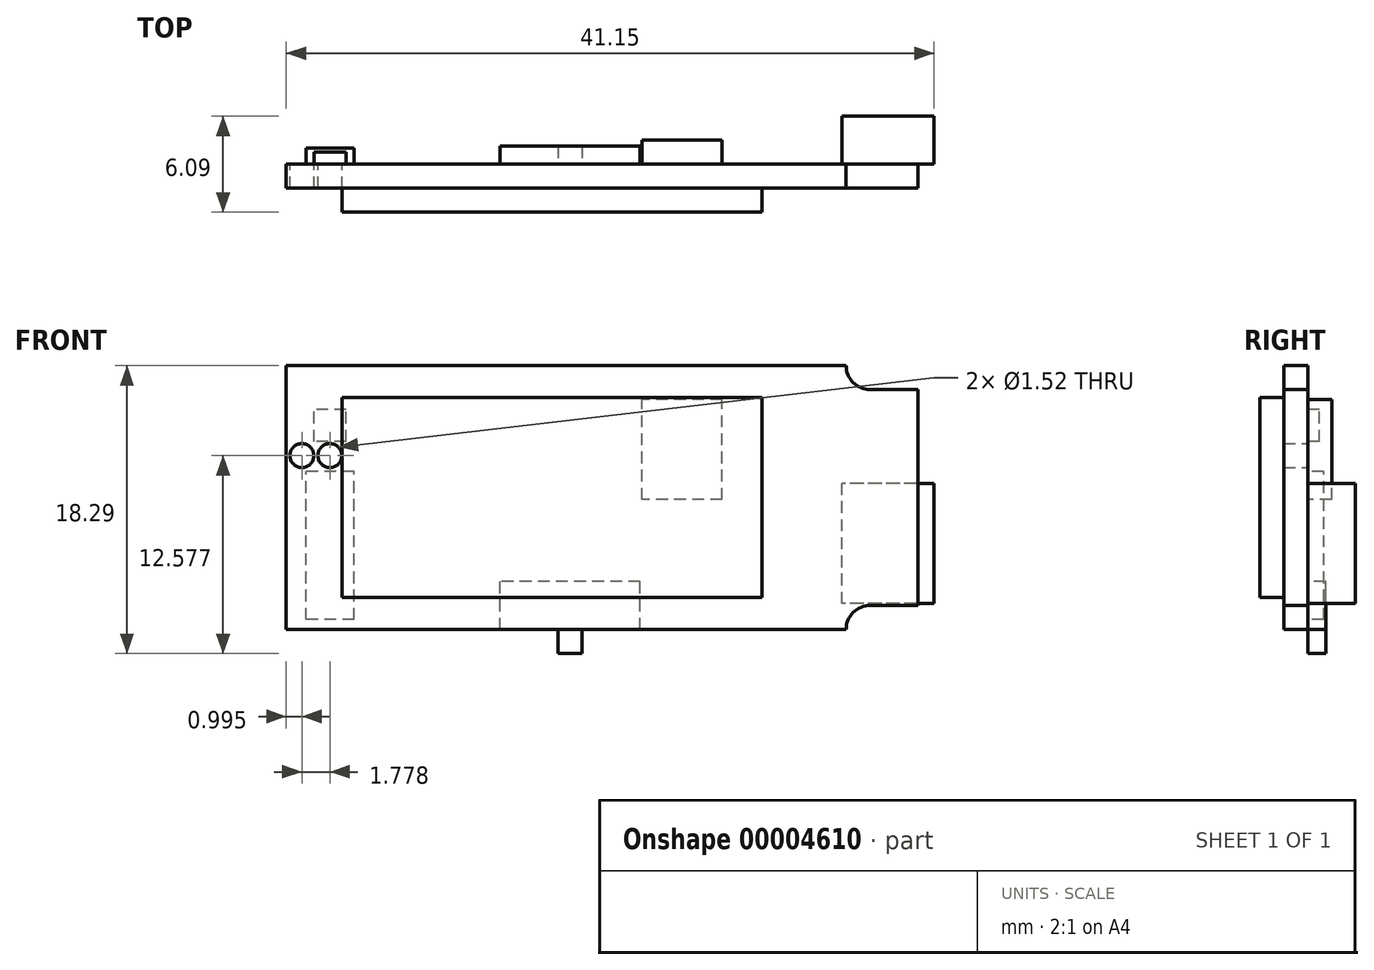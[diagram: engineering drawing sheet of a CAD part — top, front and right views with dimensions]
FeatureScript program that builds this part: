
annotation { "Feature Type Name" : "Feature", "Feature Type Description" : "" }
export const myFeature = defineFeature(function(context is Context, id is Id, definition is map)
    precondition{}
    {
        {
            var Q0;
            Q0=qCreatedBy(makeId("Front.planeOp"),FACE);
            var sketch = newSketch(context, id + "F0", { "sketchPlane" : qUnion([Q0])});
            skLineSegment(sketch, "E0.rect.bottom", {"start": v(20.07, -8.38) * mm, "end": v(-20.07, -8.38) * mm});
            skLineSegment(sketch, "E0.rect.top", {"start": v(20.07, 8.38) * mm, "end": v(-20.07, 8.38) * mm});
            skLineSegment(sketch, "E0.rect.left", {"start": v(20.07, -8.38) * mm, "end": v(20.07, 8.38) * mm});
            skLineSegment(sketch, "E0.rect.right", {"start": v(-20.07, -8.38) * mm, "end": v(-20.07, 8.38) * mm});
            skPoint(sketch, "E0.rect.middle", {"position": v(0, 0) * mm});
            skSolve(sketch);
        }
        {
            var Q0;
            Q0=makeQuery(id+"F0.imprint","IMPRINT",FACE,{"disambiguationData":[TD([[makeQuery(id+"F0.imprint","IMPRINT",EDGE,{"derivedFrom":sQuery(id+"F0.wireOp",EDGE,"E0.rect.bottom")}),-1.0]])]});
            extrude(context, id + "F1", {"entities" : qUnion([Q0]), "oppositeDirection" : true, "depth" : 1.52 * mm});
        }
        {
            var Q0;
            Q0=qCreatedBy(makeId("Front.planeOp"),FACE);
            var sketch = newSketch(context, id + "F2", { "sketchPlane" : qUnion([Q0])});
            skLineSegment(sketch, "E1.0", {"start": v(20.07, 6.86) * mm, "end": v(20.07, 8.38) * mm, "construction": true});
            skLineSegment(sketch, "E2.0", {"start": v(20.07, 8.38) * mm, "end": v(15.5, 8.38) * mm});
            skLineSegment(sketch, "E3", {"start": v(20.07, 6.86) * mm, "end": v(17.02, 6.86) * mm});
            skArc(sketch, "E4", {"start": v(15.5, 8.38) * mm, "mid": v(15.94, 7.3) * mm, "end": v(17.02, 6.86) * mm});
            skPoint(sketch, "E5.orphan", {"position": v(-20.07, 8.38) * mm});
            skPoint(sketch, "E6.orphan", {"position": v(20.07, -8.38) * mm});
            skLineSegment(sketch, "E7", {"start": v(20.07, -8.38) * mm, "end": v(20.07, -6.86) * mm});
            skLineSegment(sketch, "E8", {"start": v(20.07, -6.86) * mm, "end": v(17.02, -6.86) * mm});
            skLineSegment(sketch, "E9", {"start": v(20.07, -8.38) * mm, "end": v(15.5, -8.38) * mm});
            skArc(sketch, "E10", {"start": v(17.02, -6.86) * mm, "mid": v(15.94, -7.3) * mm, "end": v(15.5, -8.38) * mm});
            skLineSegment(sketch, "E11", {"start": v(20.07, 6.86) * mm, "end": v(20.07, 8.38) * mm});
            skSolve(sketch);
        }
        {
            var Q0;
            {Q0=qUnion([makeQuery(id+"F2.imprint","IMPRINT",FACE,{"disambiguationData":[TD([[makeQuery(id+"F2.imprint","IMPRINT",EDGE,{"derivedFrom":sQuery(id+"F2.wireOp",EDGE,"E2.0")}),1.0]])]}),makeQuery(id+"F2.imprint","IMPRINT",FACE,{"disambiguationData":[TD([[makeQuery(id+"F2.imprint","IMPRINT",EDGE,{"derivedFrom":sQuery(id+"F2.wireOp",EDGE,"E7")}),1.0]])]})]);}
            extrude(context, id + "F3", {"entities" : qUnion([Q0]), "operationType" : NewBodyOperationType.REMOVE, "endBound" : BoundingType.THROUGH_ALL, "oppositeDirection" : true, "depth" : 25.4 * mm});
        }
        {
            var Q0;
            Q0=makeQuery(id+"F1.opExtrude","CAP_FACE",FACE,{"disambiguationData":[OSD([sQuery(id+"F0.wireOp",EDGE,"E0.rect.bottom"),sQuery(id+"F0.wireOp",EDGE,"E0.rect.top"),sQuery(id+"F0.wireOp",EDGE,"E0.rect.left"),sQuery(id+"F0.wireOp",EDGE,"E0.rect.right")])],"isStart":false});
            var sketch = newSketch(context, id + "F4", { "sketchPlane" : qUnion([Q0])});
            skLineSegment(sketch, "E12.rect.bottom", {"start": v(16.5, 6.35) * mm, "end": v(-10.16, 6.35) * mm});
            skLineSegment(sketch, "E12.rect.top", {"start": v(16.5, -6.35) * mm, "end": v(-10.16, -6.35) * mm});
            skLineSegment(sketch, "E12.rect.left", {"start": v(16.5, 6.35) * mm, "end": v(16.5, -6.35) * mm});
            skLineSegment(sketch, "E12.rect.right", {"start": v(-10.16, 6.35) * mm, "end": v(-10.16, -6.35) * mm});
            skPoint(sketch, "E12.rect.middle", {"position": v(3.17, 0) * mm});
            skSolve(sketch);
        }
        {
            var Q0;
            Q0=makeQuery(id+"F4.imprint","IMPRINT",FACE,{"disambiguationData":[TD([[makeQuery(id+"F4.imprint","IMPRINT",EDGE,{"derivedFrom":sQuery(id+"F4.wireOp",EDGE,"E12.rect.bottom")}),1.0]])]});
            extrude(context, id + "F5", {"entities" : qUnion([Q0]), "operationType" : NewBodyOperationType.ADD, "oppositeDirection" : true, "depth" : 3.05 * mm});
        }
        {
            var Q0;
            Q0=makeQuery(id+"F1.opExtrude","CAP_FACE",FACE,{"disambiguationData":[OSD([sQuery(id+"F0.wireOp",EDGE,"E0.rect.bottom"),sQuery(id+"F0.wireOp",EDGE,"E0.rect.top"),sQuery(id+"F0.wireOp",EDGE,"E0.rect.left"),sQuery(id+"F0.wireOp",EDGE,"E0.rect.right")])],"isStart":true});
            var sketch = newSketch(context, id + "F6", { "sketchPlane" : qUnion([Q0])});
            skLineSegment(sketch, "E13.rect.bottom", {"start": v(21.08, -6.73) * mm, "end": v(15.24, -6.73) * mm});
            skLineSegment(sketch, "E13.rect.top", {"start": v(21.08, 0.89) * mm, "end": v(15.24, 0.89) * mm});
            skLineSegment(sketch, "E13.rect.left", {"start": v(21.08, -6.73) * mm, "end": v(21.08, 0.89) * mm});
            skLineSegment(sketch, "E13.rect.right", {"start": v(15.24, -6.73) * mm, "end": v(15.24, 0.89) * mm});
            skPoint(sketch, "E13.rect.middle", {"position": v(18.16, -2.92) * mm});
            skSolve(sketch);
        }
        {
            var Q0;
            {var subQ6=sQuery(id+"F6.wireOp",EDGE,"E13.rect.left");var subQ7=sQuery(id+"F6.wireOp",EDGE,"E13.rect.right");Q0=qUnion([makeQuery(id+"F6.imprint","IMPRINT",FACE,{"disambiguationData":[TD([[makeQuery(id+"F6.imprint","IMPRINT",EDGE,{"derivedFrom":subQ6}),1.0]])]}),makeQuery(id+"F6.imprint","IMPRINT",FACE,{"disambiguationData":[TD([[makeQuery(id+"F6.imprint","IMPRINT",EDGE,{"derivedFrom":subQ7}),-1.0]])]})]);}
            extrude(context, id + "F7", {"entities" : qUnion([Q0]), "operationType" : NewBodyOperationType.ADD, "oppositeDirection" : true, "depth" : 4.57 * mm});
        }
        {
            var Q0;
            Q0=makeQuery(id+"F7.boolean.opBoolean","MERGE",FACE,{"derivedFrom":[makeQuery(id+"F1.opExtrude","CAP_FACE",FACE,{"disambiguationData":[OSD([sQuery(id+"F0.wireOp",EDGE,"E0.rect.bottom"),sQuery(id+"F0.wireOp",EDGE,"E0.rect.top"),sQuery(id+"F0.wireOp",EDGE,"E0.rect.left"),sQuery(id+"F0.wireOp",EDGE,"E0.rect.right")])],"isStart":true}),makeQuery(id+"F7.opExtrude","CAP_FACE",FACE,{"disambiguationData":[OSD([sQuery(id+"F6.wireOp",EDGE,"E13.rect.bottom"),sQuery(id+"F6.wireOp",EDGE,"E13.rect.top"),sQuery(id+"F6.wireOp",EDGE,"E13.rect.left"),sQuery(id+"F6.wireOp",EDGE,"E13.rect.right")])],"isStart":true})]});
            var sketch = newSketch(context, id + "F8", { "sketchPlane" : qUnion([Q0])});
            skLineSegment(sketch, "E14.rect.bottom", {"start": v(-16.26, 3.56) * mm, "end": v(-18.29, 3.56) * mm});
            skLineSegment(sketch, "E14.rect.top", {"start": v(-16.26, 5.59) * mm, "end": v(-18.29, 5.59) * mm});
            skLineSegment(sketch, "E14.rect.left", {"start": v(-16.26, 3.56) * mm, "end": v(-16.26, 5.59) * mm});
            skLineSegment(sketch, "E14.rect.right", {"start": v(-18.29, 3.56) * mm, "end": v(-18.29, 5.59) * mm});
            skPoint(sketch, "E14.rect.middle", {"position": v(-17.27, 4.57) * mm});
            skSolve(sketch);
        }
        {
            var Q0;
            {var subQ6=sQuery(id+"F8.wireOp",EDGE,"E14.rect.left");var subQ7=sQuery(id+"F8.wireOp",EDGE,"E14.rect.right");Q0=qUnion([makeQuery(id+"F8.imprint","IMPRINT",FACE,{"disambiguationData":[TD([[makeQuery(id+"F8.imprint","IMPRINT",EDGE,{"derivedFrom":subQ6}),1.0]])]}),makeQuery(id+"F8.imprint","IMPRINT",FACE,{"disambiguationData":[TD([[makeQuery(id+"F8.imprint","IMPRINT",EDGE,{"derivedFrom":subQ7}),-1.0]])]})]);}
            extrude(context, id + "F9", {"entities" : qUnion([Q0]), "operationType" : NewBodyOperationType.ADD, "oppositeDirection" : true, "depth" : 2.3 * mm});
        }
        {
            var Q0;
            Q0=makeQuery(id+"F7.boolean.opBoolean","MERGE",FACE,{"derivedFrom":[makeQuery(id+"F1.opExtrude","CAP_FACE",FACE,{"disambiguationData":[OSD([sQuery(id+"F0.wireOp",EDGE,"E0.rect.bottom"),sQuery(id+"F0.wireOp",EDGE,"E0.rect.top"),sQuery(id+"F0.wireOp",EDGE,"E0.rect.left"),sQuery(id+"F0.wireOp",EDGE,"E0.rect.right")])],"isStart":true}),makeQuery(id+"F7.opExtrude","CAP_FACE",FACE,{"disambiguationData":[OSD([sQuery(id+"F6.wireOp",EDGE,"E13.rect.bottom"),sQuery(id+"F6.wireOp",EDGE,"E13.rect.top"),sQuery(id+"F6.wireOp",EDGE,"E13.rect.left"),sQuery(id+"F6.wireOp",EDGE,"E13.rect.right")])],"isStart":true})]});
            var sketch = newSketch(context, id + "F10", { "sketchPlane" : qUnion([Q0])});
            skLineSegment(sketch, "E15.rect.bottom", {"start": v(-15.75, -7.75) * mm, "end": v(-18.8, -7.75) * mm});
            skLineSegment(sketch, "E15.rect.top", {"start": v(-15.75, 1.65) * mm, "end": v(-18.8, 1.65) * mm});
            skLineSegment(sketch, "E15.rect.left", {"start": v(-15.75, -7.75) * mm, "end": v(-15.75, 1.65) * mm});
            skLineSegment(sketch, "E15.rect.right", {"start": v(-18.8, -7.75) * mm, "end": v(-18.8, 1.65) * mm});
            skPoint(sketch, "E15.rect.middle", {"position": v(-17.27, -3.05) * mm});
            skSolve(sketch);
        }
        {
            var Q0;
            {var subQ2=sQuery(id+"F10.wireOp",EDGE,"E15.rect.left");var subQ7=sQuery(id+"F10.wireOp",EDGE,"E15.rect.top");var subQ11=sQuery(id+"F10.wireOp",EDGE,"E15.rect.bottom");var subQ12=makeQuery(id+"F10.imprint","INTERSECT",VERTEX,{"derivedFrom":[subQ7,subQ2]});Q0=qUnion([makeQuery(id+"F10.imprint","IMPRINT",FACE,{"disambiguationData":[TD([[makeQuery(id+"F10.imprint","IMPRINT",EDGE,{"derivedFrom":subQ11}),-1.0]])]}),makeQuery(id+"F10.imprint","IMPRINT",FACE,{"disambiguationData":[TD([[makeQuery(id+"F10.imprint","IMPRINT",EDGE,{"disambiguationData":[TD([[subQ12,-1.0]])],"derivedFrom":subQ7}),1.0]])]})]);}
            extrude(context, id + "F11", {"entities" : qUnion([Q0]), "operationType" : NewBodyOperationType.ADD, "oppositeDirection" : true, "depth" : 2.54 * mm});
        }
        {
            var Q0;
            Q0=makeQuery(id+"F7.boolean.opBoolean","MERGE",FACE,{"derivedFrom":[makeQuery(id+"F1.opExtrude","CAP_FACE",FACE,{"disambiguationData":[OSD([sQuery(id+"F0.wireOp",EDGE,"E0.rect.bottom"),sQuery(id+"F0.wireOp",EDGE,"E0.rect.top"),sQuery(id+"F0.wireOp",EDGE,"E0.rect.left"),sQuery(id+"F0.wireOp",EDGE,"E0.rect.right")])],"isStart":true}),makeQuery(id+"F7.opExtrude","CAP_FACE",FACE,{"disambiguationData":[OSD([sQuery(id+"F6.wireOp",EDGE,"E13.rect.bottom"),sQuery(id+"F6.wireOp",EDGE,"E13.rect.top"),sQuery(id+"F6.wireOp",EDGE,"E13.rect.left"),sQuery(id+"F6.wireOp",EDGE,"E13.rect.right")])],"isStart":true})]});
            var sketch = newSketch(context, id + "F12", { "sketchPlane" : qUnion([Q0])});
            skLineSegment(sketch, "E16.rect.bottom", {"start": v(2.41, -8.38) * mm, "end": v(-1.27, -8.38) * mm});
            skLineSegment(sketch, "E16.rect.top", {"start": v(2.41, -5.33) * mm, "end": v(-6.48, -5.33) * mm});
            skLineSegment(sketch, "E16.rect.left", {"start": v(2.41, -8.38) * mm, "end": v(2.41, -5.33) * mm});
            skLineSegment(sketch, "E16.rect.right", {"start": v(-6.48, -8.38) * mm, "end": v(-6.48, -5.33) * mm});
            skPoint(sketch, "E16.rect.middle", {"position": v(-2.03, -6.86) * mm});
            skLineSegment(sketch, "E17.rect.bottom", {"start": v(-1.27, -9.9) * mm, "end": v(-2.8, -9.9) * mm});
            skLineSegment(sketch, "E17.rect.top", {"start": v(-1.27, -8.38) * mm, "end": v(-2.8, -8.38) * mm});
            skLineSegment(sketch, "E17.rect.left", {"start": v(-1.27, -9.9) * mm, "end": v(-1.27, -8.38) * mm});
            skLineSegment(sketch, "E17.rect.right", {"start": v(-2.8, -9.9) * mm, "end": v(-2.8, -8.38) * mm});
            skPoint(sketch, "E17.rect.middle", {"position": v(-2.03, -9.14) * mm});
            skLineSegment(sketch, "E18", {"start": v(-2.03, -9.14) * mm, "end": v(-2.03, -6.86) * mm, "construction": true});
            skLineSegment(sketch, "E19.trimOffspring", {"start": v(-2.8, -8.38) * mm, "end": v(-6.48, -8.38) * mm});
            skSolve(sketch);
        }
        {
            var Q0;
            {var subQ8=sQuery(id+"F12.wireOp",EDGE,"E16.rect.top");var subQ11=sQuery(id+"F12.wireOp",EDGE,"E16.rect.bottom");Q0=qUnion([makeQuery(id+"F12.imprint","IMPRINT",FACE,{"disambiguationData":[TD([[makeQuery(id+"F12.imprint","IMPRINT",EDGE,{"derivedFrom":sQuery(id+"F12.wireOp",EDGE,"E17.rect.bottom")}),-1.0]])]}),makeQuery(id+"F12.imprint","IMPRINT",FACE,{"disambiguationData":[TD([[makeQuery(id+"F12.imprint","IMPRINT",EDGE,{"derivedFrom":subQ8}),1.0]])]}),makeQuery(id+"F12.imprint","IMPRINT",FACE,{"disambiguationData":[TD([[makeQuery(id+"F12.imprint","IMPRINT",EDGE,{"derivedFrom":subQ11}),-1.0]])]})]);}
            extrude(context, id + "F13", {"entities" : qUnion([Q0]), "operationType" : NewBodyOperationType.ADD, "oppositeDirection" : true, "depth" : 2.67 * mm});
        }
        {
            var Q0;
            Q0=makeQuery(id+"F13.boolean.opBoolean","MERGE",FACE,{"derivedFrom":[makeQuery(id+"F7.boolean.opBoolean","MERGE",FACE,{"derivedFrom":[makeQuery(id+"F1.opExtrude","CAP_FACE",FACE,{"disambiguationData":[OSD([sQuery(id+"F0.wireOp",EDGE,"E0.rect.bottom"),sQuery(id+"F0.wireOp",EDGE,"E0.rect.top"),sQuery(id+"F0.wireOp",EDGE,"E0.rect.left"),sQuery(id+"F0.wireOp",EDGE,"E0.rect.right")])],"isStart":true}),makeQuery(id+"F7.opExtrude","CAP_FACE",FACE,{"disambiguationData":[OSD([sQuery(id+"F6.wireOp",EDGE,"E13.rect.bottom"),sQuery(id+"F6.wireOp",EDGE,"E13.rect.top"),sQuery(id+"F6.wireOp",EDGE,"E13.rect.left"),sQuery(id+"F6.wireOp",EDGE,"E13.rect.right")])],"isStart":true})]}),makeQuery(id+"F13.opExtrude","CAP_FACE",FACE,{"disambiguationData":[OSD([sQuery(id+"F12.wireOp",EDGE,"E16.rect.bottom"),sQuery(id+"F12.wireOp",EDGE,"E16.rect.top"),sQuery(id+"F12.wireOp",EDGE,"E16.rect.left"),sQuery(id+"F12.wireOp",EDGE,"E16.rect.right"),sQuery(id+"F12.wireOp",EDGE,"E17.rect.bottom"),sQuery(id+"F12.wireOp",EDGE,"E17.rect.left"),sQuery(id+"F12.wireOp",EDGE,"E17.rect.right"),sQuery(id+"F12.wireOp",EDGE,"E19.trimOffspring")])],"isStart":true})]});
            var sketch = newSketch(context, id + "F14", { "sketchPlane" : qUnion([Q0])});
            skLineSegment(sketch, "E20.rect.bottom", {"start": v(7.62, -0.13) * mm, "end": v(2.54, -0.13) * mm});
            skLineSegment(sketch, "E20.rect.top", {"start": v(7.62, 6.22) * mm, "end": v(2.54, 6.22) * mm});
            skLineSegment(sketch, "E20.rect.left", {"start": v(7.62, -0.13) * mm, "end": v(7.62, 6.22) * mm});
            skLineSegment(sketch, "E20.rect.right", {"start": v(2.54, -0.13) * mm, "end": v(2.54, 6.22) * mm});
            skPoint(sketch, "E20.rect.middle", {"position": v(5.08, 3.05) * mm});
            skSolve(sketch);
        }
        {
            var Q0;
            Q0=makeQuery(id+"F14.imprint","IMPRINT",FACE,{"disambiguationData":[TD([[makeQuery(id+"F14.imprint","IMPRINT",EDGE,{"derivedFrom":sQuery(id+"F14.wireOp",EDGE,"E20.rect.bottom")}),-1.0]])]});
            extrude(context, id + "F15", {"entities" : qUnion([Q0]), "operationType" : NewBodyOperationType.ADD, "oppositeDirection" : true, "depth" : 3.05 * mm});
        }
        {
            var Q0;
            Q0=makeQuery(id+"F13.boolean.opBoolean","MERGE",FACE,{"derivedFrom":[makeQuery(id+"F7.boolean.opBoolean","MERGE",FACE,{"derivedFrom":[makeQuery(id+"F1.opExtrude","CAP_FACE",FACE,{"disambiguationData":[OSD([sQuery(id+"F0.wireOp",EDGE,"E0.rect.bottom"),sQuery(id+"F0.wireOp",EDGE,"E0.rect.top"),sQuery(id+"F0.wireOp",EDGE,"E0.rect.left"),sQuery(id+"F0.wireOp",EDGE,"E0.rect.right")])],"isStart":true}),makeQuery(id+"F7.opExtrude","CAP_FACE",FACE,{"disambiguationData":[OSD([sQuery(id+"F6.wireOp",EDGE,"E13.rect.bottom"),sQuery(id+"F6.wireOp",EDGE,"E13.rect.top"),sQuery(id+"F6.wireOp",EDGE,"E13.rect.left"),sQuery(id+"F6.wireOp",EDGE,"E13.rect.right")])],"isStart":true})]}),makeQuery(id+"F13.opExtrude","CAP_FACE",FACE,{"disambiguationData":[OSD([sQuery(id+"F12.wireOp",EDGE,"E16.rect.bottom"),sQuery(id+"F12.wireOp",EDGE,"E16.rect.top"),sQuery(id+"F12.wireOp",EDGE,"E16.rect.left"),sQuery(id+"F12.wireOp",EDGE,"E16.rect.right"),sQuery(id+"F12.wireOp",EDGE,"E17.rect.bottom"),sQuery(id+"F12.wireOp",EDGE,"E17.rect.left"),sQuery(id+"F12.wireOp",EDGE,"E17.rect.right"),sQuery(id+"F12.wireOp",EDGE,"E19.trimOffspring")])],"isStart":true})]});
            var sketch = newSketch(context, id + "F16", { "sketchPlane" : qUnion([Q0])});
            skLineSegment(sketch, "E21.0", {"start": v(-2.8, -9.9) * mm, "end": v(-2.8, -8.38) * mm});
            skLineSegment(sketch, "E22.0", {"start": v(-1.27, -9.9) * mm, "end": v(-2.8, -9.9) * mm});
            skLineSegment(sketch, "E23.0", {"start": v(-1.27, -9.9) * mm, "end": v(-1.27, -8.38) * mm});
            skLineSegment(sketch, "E24.0", {"start": v(21.08, 0.89) * mm, "end": v(20.07, 0.89) * mm});
            skLineSegment(sketch, "E25.0", {"start": v(21.08, -6.73) * mm, "end": v(21.08, 0.89) * mm});
            skLineSegment(sketch, "E26.0", {"start": v(21.08, -6.73) * mm, "end": v(20.07, -6.73) * mm});
            skLineSegment(sketch, "E27", {"start": v(20.07, -6.73) * mm, "end": v(20.07, 0.89) * mm});
            skLineSegment(sketch, "E28", {"start": v(-2.8, -8.38) * mm, "end": v(-1.27, -8.38) * mm});
            skSolve(sketch);
        }
        {
            var Q0;
            {Q0=qUnion([makeQuery(id+"F16.imprint","IMPRINT",FACE,{"disambiguationData":[TD([[makeQuery(id+"F16.imprint","IMPRINT",EDGE,{"derivedFrom":sQuery(id+"F16.wireOp",EDGE,"E21.0")}),-1.0]])]}),makeQuery(id+"F16.imprint","IMPRINT",FACE,{"disambiguationData":[TD([[makeQuery(id+"F16.imprint","IMPRINT",EDGE,{"derivedFrom":sQuery(id+"F16.wireOp",EDGE,"E24.0")}),1.0]])]})]);}
            extrude(context, id + "F17", {"entities" : qUnion([Q0]), "operationType" : NewBodyOperationType.REMOVE, "oppositeDirection" : true, "depth" : 1.52 * mm});
        }
        {
            var Q0;
            Q0=makeQuery(id+"F1.opExtrude","CAP_FACE",FACE,{"disambiguationData":[OSD([sQuery(id+"F0.wireOp",EDGE,"E0.rect.bottom"),sQuery(id+"F0.wireOp",EDGE,"E0.rect.top"),sQuery(id+"F0.wireOp",EDGE,"E0.rect.left"),sQuery(id+"F0.wireOp",EDGE,"E0.rect.right")])],"isStart":false});
            var sketch = newSketch(context, id + "F18", { "sketchPlane" : qUnion([Q0])});
            skCircle(sketch, "E29", {"center": v(17.3, 2.67) * mm, "radius": 0.76 * mm});
            skCircle(sketch, "E30", {"center": v(19.08, 2.67) * mm, "radius": 0.76 * mm});
            skLineSegment(sketch, "E31", {"start": v(17.3, 2.67) * mm, "end": v(19.08, 2.67) * mm, "construction": true});
            skSolve(sketch);
        }
        {
            var Q0;
            {Q0=qUnion([makeQuery(id+"F18.imprint","IMPRINT",FACE,{"disambiguationData":[TD([[makeQuery(id+"F18.imprint","IMPRINT",EDGE,{"derivedFrom":sQuery(id+"F18.wireOp",EDGE,"E29")}),1.0]])]}),makeQuery(id+"F18.imprint","IMPRINT",FACE,{"disambiguationData":[TD([[makeQuery(id+"F18.imprint","IMPRINT",EDGE,{"derivedFrom":sQuery(id+"F18.wireOp",EDGE,"E30")}),1.0]])]})]);}
            extrude(context, id + "F19", {"entities" : qUnion([Q0]), "operationType" : NewBodyOperationType.REMOVE, "endBound" : BoundingType.THROUGH_ALL, "oppositeDirection" : true, "depth" : 25.4 * mm});
        }
    });
